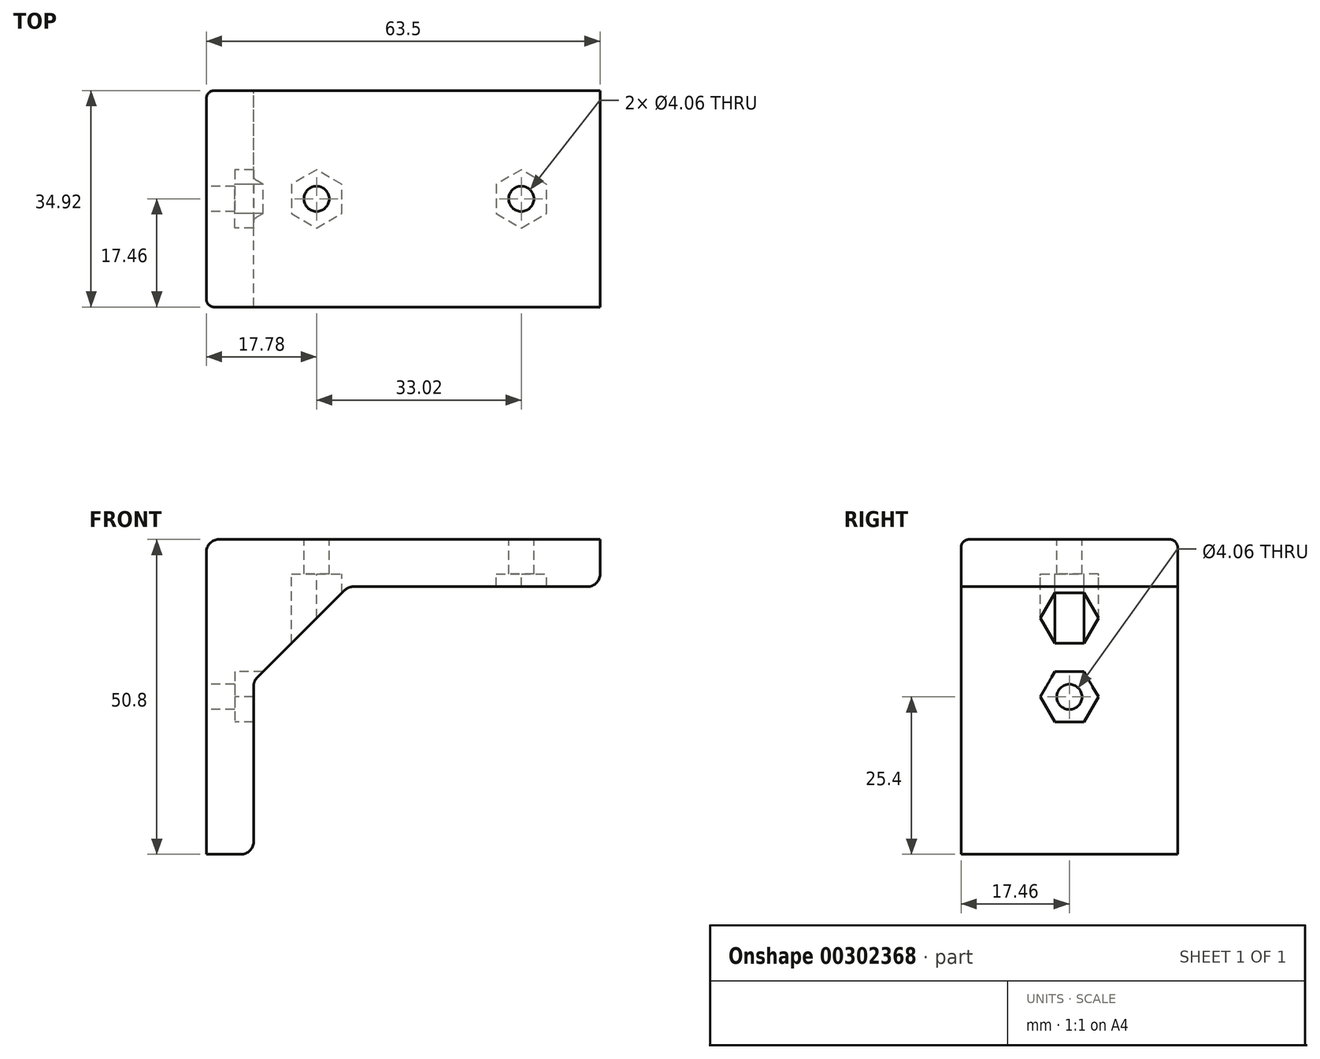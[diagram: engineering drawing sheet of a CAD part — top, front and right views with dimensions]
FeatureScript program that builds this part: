
annotation { "Feature Type Name" : "Feature", "Feature Type Description" : "" }
export const myFeature = defineFeature(function(context is Context, id is Id, definition is map)
    precondition{}
    {
        {
            var Q0;
            Q0=qCreatedBy(makeId("Front.planeOp"),FACE);
            var sketch = newSketch(context, id + "F0", { "sketchPlane" : qUnion([Q0])});
            skLineSegment(sketch, "E0.bottom", {"start": v(0, 0) * mm, "end": v(63.5, 0) * mm});
            skLineSegment(sketch, "E0.top", {"start": v(0, -50.8) * mm, "end": v(63.5, -50.8) * mm});
            skLineSegment(sketch, "E0.left", {"start": v(0, 0) * mm, "end": v(0, -50.8) * mm});
            skLineSegment(sketch, "E0.right", {"start": v(63.5, 0) * mm, "end": v(63.5, -50.8) * mm});
            skLineSegment(sketch, "E1", {"start": v(63.5, -7.62) * mm, "end": v(22.86, -7.62) * mm});
            skLineSegment(sketch, "E2", {"start": v(22.86, -7.62) * mm, "end": v(7.62, -22.86) * mm});
            skLineSegment(sketch, "E3", {"start": v(7.62, -22.86) * mm, "end": v(7.62, -50.8) * mm});
            skSolve(sketch);
        }
        {
            var Q0;
            {var subQ1=sQuery(id+"F0.wireOp",EDGE,"E0.bottom");Q0=makeQuery(id+"F0.imprint","IMPRINT",FACE,{"disambiguationData":[TD([[makeQuery(id+"F0.imprint","IMPRINT",EDGE,{"derivedFrom":subQ1}),-1.0]])]});}
            extrude(context, id + "F1", {"entities" : qUnion([Q0]), "endBound" : BoundingType.SYMMETRIC, "depth" : 34.92 * mm});
        }
        {
            var Q0;
            Q0=makeQuery(id+"F1.opExtrude","SWEPT_FACE",FACE,{"disambiguationData":[OSD([sQuery(id+"F0.wireOp",EDGE,"E0.bottom")])]});
            var sketch = newSketch(context, id + "F2", { "sketchPlane" : qUnion([Q0])});
            skCircle(sketch, "E4", {"center": v(17.78, 0) * mm, "radius": 2.03 * mm});
            skCircle(sketch, "E5", {"center": v(50.8, 0) * mm, "radius": 2.03 * mm});
            skCircle(sketch, "E6.cCircle", {"center": v(17.78, 0) * mm, "radius": 4.06 * mm, "construction": true});
            skLineSegment(sketch, "E6.0", {"start": v(17.78, 4.7) * mm, "end": v(21.84, 2.35) * mm});
            skLineSegment(sketch, "E6.1", {"start": v(21.84, 2.35) * mm, "end": v(21.84, -2.35) * mm});
            skLineSegment(sketch, "E6.2", {"start": v(21.84, -2.35) * mm, "end": v(17.78, -4.7) * mm});
            skLineSegment(sketch, "E6.3", {"start": v(17.78, -4.7) * mm, "end": v(13.72, -2.35) * mm});
            skLineSegment(sketch, "E6.4", {"start": v(13.72, -2.35) * mm, "end": v(13.72, 2.35) * mm});
            skLineSegment(sketch, "E6.5", {"start": v(13.72, 2.35) * mm, "end": v(17.78, 4.7) * mm});
            skPoint(sketch, "E6.0.midPoint", {"position": v(17.78, 4.06) * mm});
            skCircle(sketch, "E7.cCircle", {"center": v(50.8, 0) * mm, "radius": 4.06 * mm, "construction": true});
            skLineSegment(sketch, "E7.0", {"start": v(50.8, 4.7) * mm, "end": v(54.86, 2.35) * mm});
            skLineSegment(sketch, "E7.1", {"start": v(54.86, 2.35) * mm, "end": v(54.86, -2.35) * mm});
            skLineSegment(sketch, "E7.2", {"start": v(54.86, -2.35) * mm, "end": v(50.8, -4.7) * mm});
            skLineSegment(sketch, "E7.3", {"start": v(50.8, -4.7) * mm, "end": v(46.74, -2.35) * mm});
            skLineSegment(sketch, "E7.4", {"start": v(46.74, -2.35) * mm, "end": v(46.74, 2.35) * mm});
            skLineSegment(sketch, "E7.5", {"start": v(46.74, 2.35) * mm, "end": v(50.8, 4.7) * mm});
            skPoint(sketch, "E7.0.midPoint", {"position": v(50.8, 4.06) * mm});
            skSolve(sketch);
        }
        {
            var Q0;
            Q0=makeQuery(id+"F1.opExtrude","SWEPT_FACE",FACE,{"disambiguationData":[OSD([sQuery(id+"F0.wireOp",EDGE,"E0.left")])]});
            var sketch = newSketch(context, id + "F3", { "sketchPlane" : qUnion([Q0])});
            skCircle(sketch, "E8", {"center": v(0, -25.4) * mm, "radius": 2.03 * mm});
            skCircle(sketch, "E9.cCircle", {"center": v(0, -25.4) * mm, "radius": 4.06 * mm, "construction": true});
            skLineSegment(sketch, "E9.0", {"start": v(2.35, -29.46) * mm, "end": v(-2.35, -29.46) * mm});
            skLineSegment(sketch, "E9.1", {"start": v(-2.35, -29.46) * mm, "end": v(-4.7, -25.4) * mm});
            skLineSegment(sketch, "E9.2", {"start": v(-4.7, -25.4) * mm, "end": v(-2.35, -21.34) * mm});
            skLineSegment(sketch, "E9.3", {"start": v(-2.35, -21.34) * mm, "end": v(2.35, -21.34) * mm});
            skLineSegment(sketch, "E9.4", {"start": v(2.35, -21.34) * mm, "end": v(4.7, -25.4) * mm});
            skLineSegment(sketch, "E9.5", {"start": v(4.7, -25.4) * mm, "end": v(2.35, -29.46) * mm});
            skPoint(sketch, "E9.0.midPoint", {"position": v(-4.06, -25.4) * mm});
            skSolve(sketch);
        }
        {
            var Q0;
            Q0=makeQuery(id+"F2.imprint","IMPRINT",FACE,{"disambiguationData":[TD([[makeQuery(id+"F2.imprint","IMPRINT",EDGE,{"derivedFrom":sQuery(id+"F2.wireOp",EDGE,"E4")}),1.0]])]});
            var Q1;
            Q1=makeQuery(id+"F2.imprint","IMPRINT",FACE,{"disambiguationData":[TD([[makeQuery(id+"F2.imprint","IMPRINT",EDGE,{"derivedFrom":sQuery(id+"F2.wireOp",EDGE,"E5")}),1.0]])]});
            extrude(context, id + "F4", {"entities" : qUnion([Q0, Q1]), "operationType" : NewBodyOperationType.REMOVE, "oppositeDirection" : true, "depth" : 25.4 * mm});
        }
        {
            var Q0;
            Q0=makeQuery(id+"F2.imprint","IMPRINT",FACE,{"disambiguationData":[TD([[makeQuery(id+"F2.imprint","IMPRINT",EDGE,{"derivedFrom":sQuery(id+"F2.wireOp",EDGE,"E4")}),-1.0]])]});
            var Q1;
            Q1=makeQuery(id+"F2.imprint","IMPRINT",FACE,{"disambiguationData":[TD([[makeQuery(id+"F2.imprint","IMPRINT",EDGE,{"derivedFrom":sQuery(id+"F2.wireOp",EDGE,"E5")}),-1.0]])]});
            extrude(context, id + "F5", {"entities" : qUnion([Q0, Q1]), "operationType" : NewBodyOperationType.REMOVE, "oppositeDirection" : true, "depth" : 25.4 * mm, "hasSecondDirection" : true, "secondDirectionOppositeDirection" : true, "secondDirectionDepth" : 5.6 * mm});
        }
        {
            var Q0;
            Q0=makeQuery(id+"F3.imprint","IMPRINT",FACE,{"disambiguationData":[TD([[makeQuery(id+"F3.imprint","IMPRINT",EDGE,{"derivedFrom":sQuery(id+"F3.wireOp",EDGE,"E8")}),1.0]])]});
            extrude(context, id + "F6", {"entities" : qUnion([Q0]), "operationType" : NewBodyOperationType.REMOVE, "oppositeDirection" : true, "depth" : 25.4 * mm});
        }
        {
            var Q0;
            Q0=makeQuery(id+"F3.imprint","IMPRINT",FACE,{"disambiguationData":[TD([[makeQuery(id+"F3.imprint","IMPRINT",EDGE,{"derivedFrom":sQuery(id+"F3.wireOp",EDGE,"E8")}),-1.0]])]});
            extrude(context, id + "F7", {"entities" : qUnion([Q0]), "operationType" : NewBodyOperationType.REMOVE, "oppositeDirection" : true, "depth" : 25.4 * mm, "hasSecondDirection" : true, "secondDirectionOppositeDirection" : true, "secondDirectionDepth" : 4.57 * mm});
        }
        {
            var Q0;
            Q0=makeQuery(id+"F1.opExtrude","SWEPT_EDGE",EDGE,{"disambiguationData":[OSD([sQuery(id+"F0.wireOp",EDGE,"E0.right"),sQuery(id+"F0.wireOp",EDGE,"E1")])]});
            var Q1;
            Q1=makeQuery(id+"F1.opExtrude","SWEPT_EDGE",EDGE,{"disambiguationData":[OSD([sQuery(id+"F0.wireOp",EDGE,"E0.top"),sQuery(id+"F0.wireOp",EDGE,"E3")])]});
            var Q2;
            {var subQ0=sQuery(id+"F0.wireOp",EDGE,"E3");var subQ1=sQuery(id+"F0.wireOp",EDGE,"E2");Q2=makeQuery(id+"F6.boolean.opBoolean","SPLIT",EDGE,{"disambiguationData":[TD([makeQuery(id+"F1.opExtrude","CAP_FACE",FACE,{"disambiguationData":[OSD([sQuery(id+"F0.wireOp",EDGE,"E0.bottom"),sQuery(id+"F0.wireOp",EDGE,"E0.top"),sQuery(id+"F0.wireOp",EDGE,"E0.left"),sQuery(id+"F0.wireOp",EDGE,"E0.right"),sQuery(id+"F0.wireOp",EDGE,"E1"),subQ1,subQ0])],"isStart":true})])],"derivedFrom":makeQuery(id+"F1.opExtrude","SWEPT_EDGE",EDGE,{"disambiguationData":[OSD([subQ1,subQ0])]})});}
            var Q3;
            {var subQ0=sQuery(id+"F0.wireOp",EDGE,"E3");var subQ1=sQuery(id+"F0.wireOp",EDGE,"E2");Q3=makeQuery(id+"F6.boolean.opBoolean","SPLIT",EDGE,{"disambiguationData":[TD([makeQuery(id+"F1.opExtrude","CAP_FACE",FACE,{"disambiguationData":[OSD([sQuery(id+"F0.wireOp",EDGE,"E0.bottom"),sQuery(id+"F0.wireOp",EDGE,"E0.top"),sQuery(id+"F0.wireOp",EDGE,"E0.left"),sQuery(id+"F0.wireOp",EDGE,"E0.right"),sQuery(id+"F0.wireOp",EDGE,"E1"),subQ1,subQ0])],"isStart":false})])],"derivedFrom":makeQuery(id+"F1.opExtrude","SWEPT_EDGE",EDGE,{"disambiguationData":[OSD([subQ1,subQ0])]})});}
            var Q4;
            Q4=makeQuery(id+"F1.opExtrude","SWEPT_EDGE",EDGE,{"disambiguationData":[OSD([sQuery(id+"F0.wireOp",EDGE,"E1"),sQuery(id+"F0.wireOp",EDGE,"E2")])]});
            var Q5;
            Q5=makeQuery(id+"F1.opExtrude","SWEPT_EDGE",EDGE,{"disambiguationData":[OSD([sQuery(id+"F0.wireOp",EDGE,"E0.bottom"),sQuery(id+"F0.wireOp",EDGE,"E0.left")])]});
            fillet(context, id + "F8", {"entities" : qUnion([Q0, Q1, Q2, Q3, Q4, Q5]), "radius" : 2.03 * mm, "tangentPropagation" : true, "allowEdgeOverflow" : false});
        }
        {
            var Q0;
            Q0=makeQuery(id+"F1.opExtrude","CAP_EDGE",EDGE,{"disambiguationData":[OSD([sQuery(id+"F0.wireOp",EDGE,"E0.bottom")])],"isStart":false});
            var Q1;
            Q1=makeQuery(id+"F1.opExtrude","CAP_EDGE",EDGE,{"disambiguationData":[OSD([sQuery(id+"F0.wireOp",EDGE,"E0.bottom")])],"isStart":true});
            fillet(context, id + "F9", {"entities" : qUnion([Q0, Q1]), "radius" : 1.27 * mm, "tangentPropagation" : true, "allowEdgeOverflow" : false});
        }
    });
